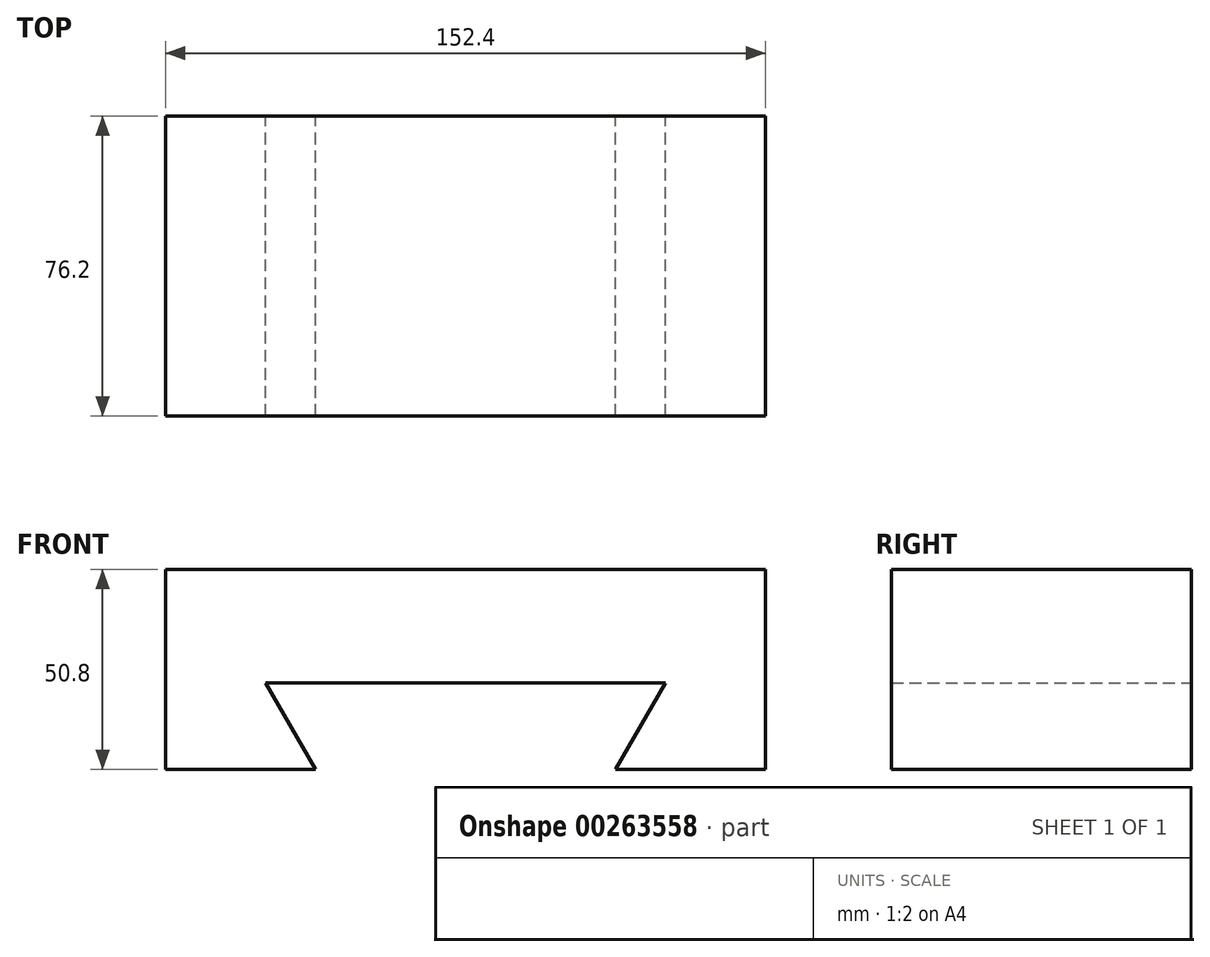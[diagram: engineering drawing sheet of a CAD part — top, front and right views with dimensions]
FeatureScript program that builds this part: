
annotation { "Feature Type Name" : "Feature", "Feature Type Description" : "" }
export const myFeature = defineFeature(function(context is Context, id is Id, definition is map)
    precondition{}
    {
        {
            var Q0;
            Q0=qCreatedBy(makeId("Front.planeOp"),FACE);
            var sketch = newSketch(context, id + "F0", { "sketchPlane" : qUnion([Q0])});
            skLineSegment(sketch, "E0", {"start": v(-53.19, 42.58) * mm, "end": v(-53.19, -8.22) * mm});
            skLineSegment(sketch, "E1", {"start": v(-53.19, -8.22) * mm, "end": v(-15.09, -8.22) * mm});
            skLineSegment(sketch, "E2", {"start": v(-15.09, -8.22) * mm, "end": v(-27.79, 13.78) * mm});
            skLineSegment(sketch, "E3", {"start": v(-27.79, 13.78) * mm, "end": v(73.81, 13.78) * mm});
            skLineSegment(sketch, "E4", {"start": v(73.81, 13.78) * mm, "end": v(61.11, -8.22) * mm});
            skLineSegment(sketch, "E5", {"start": v(61.11, -8.22) * mm, "end": v(99.21, -8.22) * mm});
            skLineSegment(sketch, "E6", {"start": v(99.21, -8.22) * mm, "end": v(99.21, 42.58) * mm});
            skLineSegment(sketch, "E7", {"start": v(99.21, 42.58) * mm, "end": v(-53.19, 42.58) * mm});
            skSolve(sketch);
        }
        {
            var Q0;
            Q0=makeQuery(id+"F0.imprint","IMPRINT",FACE,{"disambiguationData":[TD([[makeQuery(id+"F0.imprint","IMPRINT",EDGE,{"derivedFrom":sQuery(id+"F0.wireOp",EDGE,"E0")}),1.0]])]});
            extrude(context, id + "F1", {"entities" : qUnion([Q0]), "depth" : 76.2 * mm});
        }
    });
